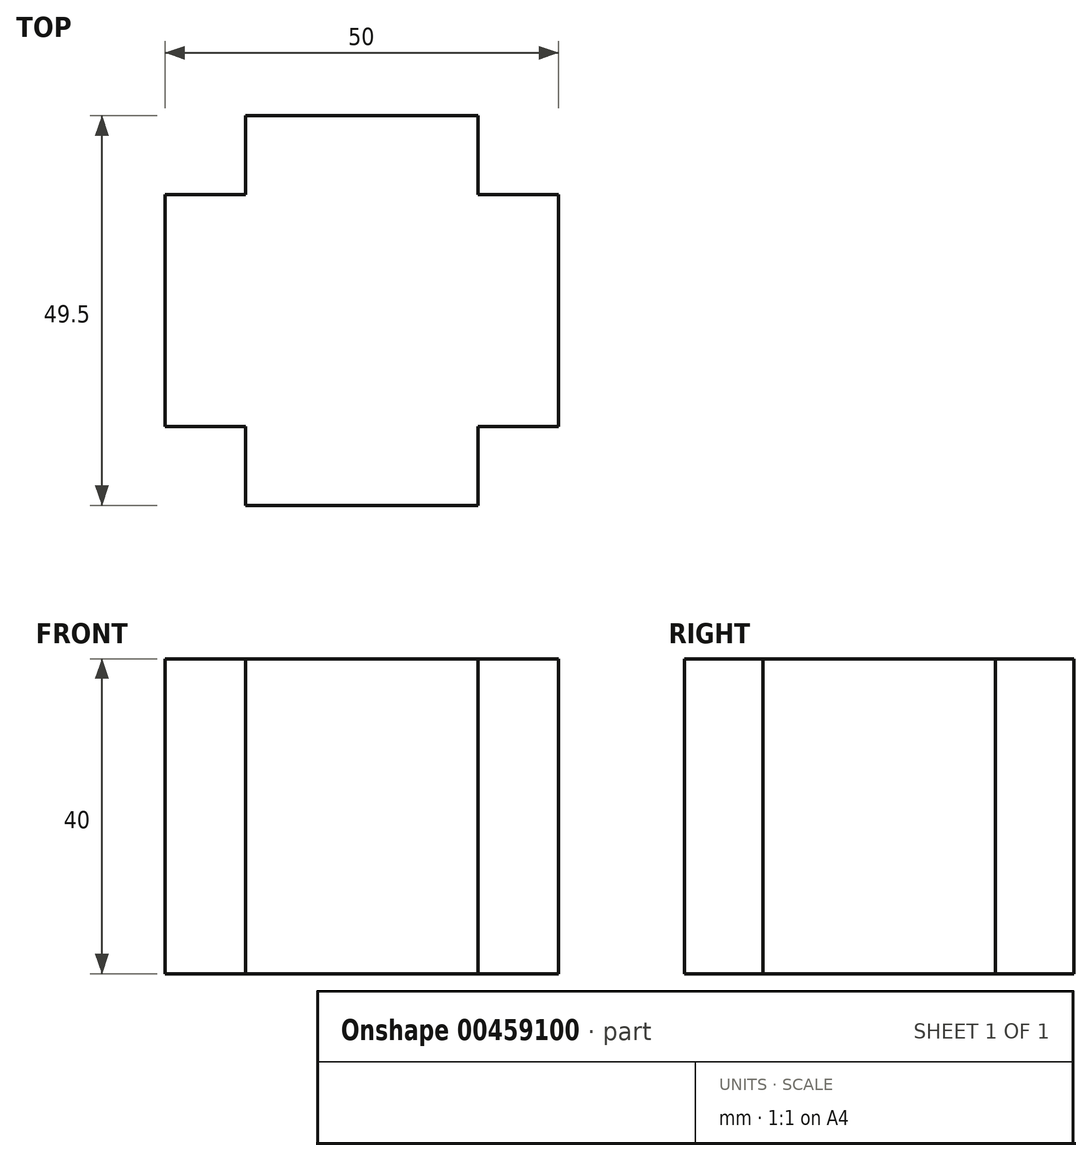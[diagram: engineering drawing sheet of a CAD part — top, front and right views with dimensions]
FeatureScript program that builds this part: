
annotation { "Feature Type Name" : "Feature", "Feature Type Description" : "" }
export const myFeature = defineFeature(function(context is Context, id is Id, definition is map)
    precondition{}
    {
        {
            var Q0;
            Q0=qCreatedBy(makeId("Top.planeOp"),FACE);
            var sketch = newSketch(context, id + "F0", { "sketchPlane" : qUnion([Q0])});
            skLineSegment(sketch, "E0.bottom", {"start": v(-150, 75) * mm, "end": v(150, 75) * mm});
            skLineSegment(sketch, "E0.top", {"start": v(-150, -75) * mm, "end": v(150, -75) * mm});
            skLineSegment(sketch, "E0.left", {"start": v(-150, 75) * mm, "end": v(-150, -75) * mm});
            skLineSegment(sketch, "E0.right", {"start": v(150, 75) * mm, "end": v(150, -75) * mm});
            skLineSegment(sketch, "E1.bottom", {"start": v(-2.5, 24.1) * mm, "end": v(2.5, 24.1) * mm});
            skLineSegment(sketch, "E1.top", {"start": v(-2.5, -24.1) * mm, "end": v(2.5, -24.1) * mm});
            skLineSegment(sketch, "E1.left", {"start": v(-2.5, 24.1) * mm, "end": v(-2.5, -24.1) * mm});
            skLineSegment(sketch, "E1.right", {"start": v(2.5, 24.1) * mm, "end": v(2.5, -24.1) * mm});
            skLineSegment(sketch, "E2", {"start": v(-150, 24.1) * mm, "end": v(-2.5, 24.1) * mm, "construction": true});
            skLineSegment(sketch, "E3", {"start": v(2.5, 24.1) * mm, "end": v(150, 24.1) * mm, "construction": true});
            skLineSegment(sketch, "E4", {"start": v(2.5, -24.1) * mm, "end": v(2.5, -75) * mm, "construction": true});
            skLineSegment(sketch, "E5", {"start": v(2.5, 24.1) * mm, "end": v(2.5, 75) * mm, "construction": true});
            skLineSegment(sketch, "E6", {"start": v(2.5, 0) * mm, "end": v(-2.5, 0) * mm, "construction": true});
            skLineSegment(sketch, "E7", {"start": v(0, 24.1) * mm, "end": v(0, -24.1) * mm, "construction": true});
            skSolve(sketch);
        }
        {
            var Q0;
            Q0=makeQuery(id+"F0.imprint","IMPRINT",FACE,{"disambiguationData":[TD([[makeQuery(id+"F0.imprint","IMPRINT",EDGE,{"derivedFrom":sQuery(id+"F0.wireOp",EDGE,"E0.bottom")}),-1.0]])]});
            cPlane(context, id + "F1", {"entities" : qUnion([Q0]), "cplaneType" : CPlaneType.OFFSET, "offset" : 0 * mm, "width" : 150 * mm, "height" : 150 * mm});
        }
        {
            var Q0;
            Q0=qCreatedBy(id+"F1.planeOp",FACE);
            var sketch = newSketch(context, id + "F2", { "sketchPlane" : qUnion([Q0])});
            skLineSegment(sketch, "E8", {"start": v(-30, 15) * mm, "end": v(-30, 35) * mm});
            skLineSegment(sketch, "E9", {"start": v(-30, 35) * mm, "end": v(-80, 35) * mm});
            skLineSegment(sketch, "E10", {"start": v(-80, 35) * mm, "end": v(-80, 15) * mm});
            skLineSegment(sketch, "E11", {"start": v(-80, 15) * mm, "end": v(-70, 15) * mm});
            skLineSegment(sketch, "E12", {"start": v(-70, 15) * mm, "end": v(-70, 25) * mm});
            skLineSegment(sketch, "E13", {"start": v(-70, 25) * mm, "end": v(-40, 25) * mm});
            skLineSegment(sketch, "E14", {"start": v(-40, 25) * mm, "end": v(-40, 15) * mm});
            skLineSegment(sketch, "E15", {"start": v(-40, 15) * mm, "end": v(-30, 15) * mm});
            skLineSegment(sketch, "E16", {"start": v(-55, 25) * mm, "end": v(-55, 35) * mm, "construction": true});
            skLineSegment(sketch, "E17.MirrorCS", {"start": v(-80, -35) * mm, "end": v(-80, -15) * mm});
            skLineSegment(sketch, "E18.MirrorCS", {"start": v(-80, -15) * mm, "end": v(-70, -15) * mm});
            skLineSegment(sketch, "E19.MirrorCS", {"start": v(-70, -15) * mm, "end": v(-70, -25) * mm});
            skLineSegment(sketch, "E20.MirrorCS", {"start": v(-70, -25) * mm, "end": v(-40, -25) * mm});
            skLineSegment(sketch, "E21.MirrorCS", {"start": v(-40, -25) * mm, "end": v(-40, -15) * mm});
            skLineSegment(sketch, "E22.MirrorCS", {"start": v(-40, -15) * mm, "end": v(-30, -15) * mm});
            skLineSegment(sketch, "E23.MirrorCS", {"start": v(-30, -15) * mm, "end": v(-30, -35) * mm});
            skLineSegment(sketch, "E24.MirrorCS", {"start": v(-30, -35) * mm, "end": v(-80, -35) * mm});
            skSolve(sketch);
        }
        {
            var Q0;
            Q0=qCreatedBy(makeId("Front.planeOp"),FACE);
            var sketch = newSketch(context, id + "F3", { "sketchPlane" : qUnion([Q0])});
            skLineSegment(sketch, "E25", {"start": v(-152.06, -3.5) * mm, "end": v(-87.5, -3.5) * mm});
            skLineSegment(sketch, "E26", {"start": v(-87.5, -3.5) * mm, "end": v(-87.5, -2) * mm});
            skFitSpline(sketch, "E27", {"points": [v(-87.5, -2) * mm, v(-82.5, 0) * mm], "startDerivative": vector(5.33, 0.16) * mm, "endDerivative": vector(2.89, 4.52) * mm});
            skLineSegment(sketch, "E28", {"start": v(-82.5, 0) * mm, "end": v(-35.5, 0) * mm});
            skFitSpline(sketch, "E29", {"points": [v(-35.5, 0) * mm, v(-30, -4) * mm], "startDerivative": vector(6.72, -0.05) * mm, "endDerivative": vector(2.87, -8.37) * mm});
            skLineSegment(sketch, "E30", {"start": v(-30, -4) * mm, "end": v(-26.5, -4) * mm});
            skLineSegment(sketch, "E31", {"start": v(-26.5, -4) * mm, "end": v(-24.5, -8.4) * mm});
            skLineSegment(sketch, "E32", {"start": v(-24.5, -8.4) * mm, "end": v(-18.4, -8.4) * mm});
            skLineSegment(sketch, "E33", {"start": v(-18.4, -8.4) * mm, "end": v(-16.6, -6) * mm});
            skLineSegment(sketch, "E34", {"start": v(-16.6, -6) * mm, "end": v(-4.8, -6) * mm});
            skLineSegment(sketch, "E35", {"start": v(-4.8, -6) * mm, "end": v(-0.3, -3.19) * mm});
            skLineSegment(sketch, "E36", {"start": v(-0.3, -3.19) * mm, "end": v(-0.3, 12.2) * mm});
            skLineSegment(sketch, "E37", {"start": v(-0.3, 12.2) * mm, "end": v(0.3, 12.2) * mm});
            skLineSegment(sketch, "E38", {"start": v(0.3, 12.2) * mm, "end": v(0.3, -3.19) * mm});
            skLineSegment(sketch, "E39", {"start": v(0.3, -3.19) * mm, "end": v(5.2, -6) * mm});
            skLineSegment(sketch, "E40", {"start": v(-152.06, -3.5) * mm, "end": v(-152.06, -10) * mm});
            skLineSegment(sketch, "E41", {"start": v(-152.06, -10) * mm, "end": v(5.2, -10) * mm});
            skLineSegment(sketch, "E42", {"start": v(5.2, -10) * mm, "end": v(5.2, -6) * mm});
            skLineSegment(sketch, "E43", {"start": v(0, 12.2) * mm, "end": v(0, -10) * mm, "construction": true});
            skSolve(sketch);
        }
        {
            var Q0;
            Q0=qCreatedBy(makeId("Top.planeOp"),FACE);
            var sketch = newSketch(context, id + "F4", { "sketchPlane" : qUnion([Q0])});
            skLineSegment(sketch, "E44", {"start": v(-80, 14.75) * mm, "end": v(-69.75, 14.75) * mm});
            skLineSegment(sketch, "E45", {"start": v(-69.75, 14.75) * mm, "end": v(-69.75, 24.75) * mm});
            skLineSegment(sketch, "E46", {"start": v(-69.75, 24.75) * mm, "end": v(-40.25, 24.75) * mm});
            skLineSegment(sketch, "E47", {"start": v(-40.25, 24.75) * mm, "end": v(-40.25, 14.75) * mm});
            skLineSegment(sketch, "E48", {"start": v(-40.25, 14.75) * mm, "end": v(-30, 14.75) * mm});
            skLineSegment(sketch, "E49", {"start": v(-30, 14.75) * mm, "end": v(-30, 0) * mm});
            skLineSegment(sketch, "E50", {"start": v(-30, 0) * mm, "end": v(-80, 0) * mm});
            skLineSegment(sketch, "E51", {"start": v(-80, 0) * mm, "end": v(-80, 14.75) * mm});
            skLineSegment(sketch, "E52.MirrorCS", {"start": v(-30, -14.75) * mm, "end": v(-30, 0) * mm});
            skLineSegment(sketch, "E53.MirrorCS", {"start": v(-40.25, -14.75) * mm, "end": v(-30, -14.75) * mm});
            skLineSegment(sketch, "E54.MirrorCS", {"start": v(-40.25, -24.75) * mm, "end": v(-40.25, -14.75) * mm});
            skLineSegment(sketch, "E55.MirrorCS", {"start": v(-69.75, -24.75) * mm, "end": v(-40.25, -24.75) * mm});
            skLineSegment(sketch, "E56.MirrorCS", {"start": v(-69.75, -14.75) * mm, "end": v(-69.75, -24.75) * mm});
            skLineSegment(sketch, "E57.MirrorCS", {"start": v(-80, -14.75) * mm, "end": v(-69.75, -14.75) * mm});
            skLineSegment(sketch, "E58.MirrorCS", {"start": v(-80, 0) * mm, "end": v(-80, -14.75) * mm});
            skSolve(sketch);
        }
        {
            var Q0;
            Q0=makeQuery(id+"F4.imprint","IMPRINT",FACE,{"disambiguationData":[TD([[makeQuery(id+"F4.imprint","IMPRINT",EDGE,{"derivedFrom":sQuery(id+"F4.wireOp",EDGE,"E50")}),1.0]])]});
            extrude(context, id + "F5", {"entities" : qUnion([Q0]), "oppositeDirection" : true, "depth" : 40 * mm});
        }
        {
            var Q0;
            Q0 = qSketchRegion(id + "F4", true);
            extrude(context, id + "F6", {"entities" : qUnion([Q0]), "operationType" : NewBodyOperationType.ADD, "oppositeDirection" : true, "depth" : 40 * mm});
        }
    });
